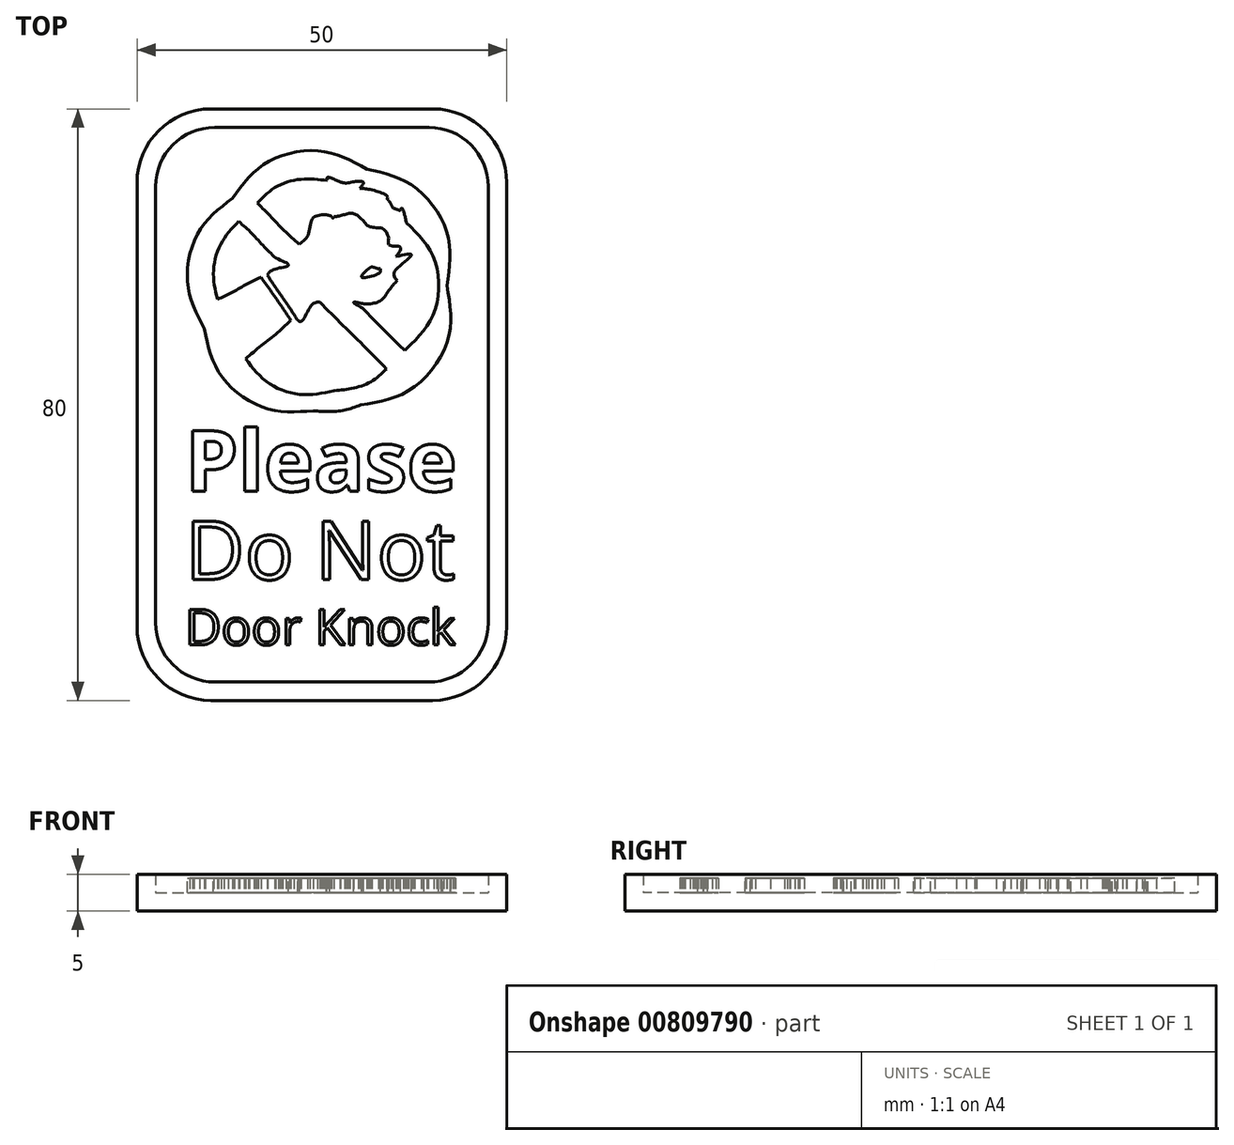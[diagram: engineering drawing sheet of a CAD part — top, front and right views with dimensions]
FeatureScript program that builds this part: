
annotation { "Feature Type Name" : "Feature", "Feature Type Description" : "" }
export const myFeature = defineFeature(function(context is Context, id is Id, definition is map)
    precondition{}
    {
        {
            var Q0;
            Q0=qCreatedBy(makeId("Top.planeOp"),FACE);
            var sketch = newSketch(context, id + "F0", { "sketchPlane" : qUnion([Q0])});
            skLineSegment(sketch, "E0.bottom", {"start": v(-25, 25) * mm, "end": v(25, 25) * mm});
            skLineSegment(sketch, "E0.top", {"start": v(-25, -55) * mm, "end": v(25, -55) * mm});
            skLineSegment(sketch, "E0.left", {"start": v(-25, 25) * mm, "end": v(-25, -55) * mm});
            skLineSegment(sketch, "E0.right", {"start": v(25, 25) * mm, "end": v(25, -55) * mm});
            skLineSegment(sketch, "E1", {"start": v(-25, 0) * mm, "end": v(25, 0) * mm});
            skSolve(sketch);
        }
        {
            var Q0;
            Q0 = qSketchRegion(id + "F0", true);
            extrude(context, id + "F1", {"entities" : qUnion([Q0]), "depth" : 5 * mm, "offsetDistance" : 25 * mm});
        }
        {
            var Q0;
            {var subQ0=sQuery(id+"F0.wireOp",EDGE,"E0.left");var subQ1=sQuery(id+"F0.wireOp",EDGE,"E0.top");var subQ2=sQuery(id+"F0.wireOp",EDGE,"E0.right");var subQ3=sQuery(id+"F0.wireOp",EDGE,"E0.bottom");Q0=makeQuery(id+"F8.boolean.opBoolean","SPLIT",FACE,{"disambiguationData":[TD([makeQuery(id+"F1.opExtrude","SWEPT_FACE",FACE,{"disambiguationData":[OSD([subQ3])]})])],"derivedFrom":makeQuery(id+"F1.opExtrude","CAP_FACE",FACE,{"disambiguationData":[OSD([subQ3,subQ1,subQ0,subQ2])],"isStart":false})});}
            shell(context, id + "F2", {"entities" : qUnion([Q0]), "thickness" : 2.5 * mm});
        }
        {
            var Q0;
            Q0=makeQuery(id+"F2.opShell","OFFSET_FACE",FACE,{"disambiguationData":[OSD([sQuery(id+"F0.wireOp",EDGE,"E0.bottom"),sQuery(id+"F0.wireOp",EDGE,"E0.top"),sQuery(id+"F0.wireOp",EDGE,"E0.left"),sQuery(id+"F0.wireOp",EDGE,"E0.right")])]});
            var sketch = newSketch(context, id + "F3", { "sketchPlane" : qUnion([Q0])});
            skText(sketch, "E2", { "text": "Please", "fontName": "OpenSans-Bold.ttf"});
            skText(sketch, "E3", { "text": "Do Not", "fontName": "OpenSans-Regular.ttf"});
            skText(sketch, "E4", { "text": "Door Knock", "fontName": "OpenSans-Regular.ttf"});
            const initialGuessF3  = {"E2": [-0.0185, -0.0267, 1, 0, 0.00823], "E3": [-0.0185, -0.03865, 1, 0, 0.00796], "E4": [-0.0185, -0.0475, 1, 0, 0.00485]};
            skSetInitialGuess(sketch, initialGuessF3);
            skSolve(sketch);
        }
        {
            var Q0;
            Q0 = qSketchRegion(id + "F3", true);
            extrude(context, id + "F4", {"entities" : qUnion([Q0]), "operationType" : NewBodyOperationType.ADD, "depth" : 2 * mm, "offsetDistance" : 25 * mm});
        }
        {
            var Q0;
            Q0=makeQuery(id+"F2.opShell","OFFSET_EDGE",EDGE,{"disambiguationData":[OSD([sQuery(id+"F0.wireOp",EDGE,"E0.bottom"),sQuery(id+"F0.wireOp",EDGE,"E0.left")])]});
            var Q1;
            Q1=makeQuery(id+"F2.opShell","OFFSET_EDGE",EDGE,{"disambiguationData":[OSD([sQuery(id+"F0.wireOp",EDGE,"E0.bottom"),sQuery(id+"F0.wireOp",EDGE,"E0.right")])]});
            var Q2;
            Q2=makeQuery(id+"F2.opShell","OFFSET_EDGE",EDGE,{"disambiguationData":[OSD([sQuery(id+"F0.wireOp",EDGE,"E0.top"),sQuery(id+"F0.wireOp",EDGE,"E0.right")])]});
            var Q3;
            Q3=makeQuery(id+"F2.opShell","OFFSET_EDGE",EDGE,{"disambiguationData":[OSD([sQuery(id+"F0.wireOp",EDGE,"E0.top"),sQuery(id+"F0.wireOp",EDGE,"E0.left")])]});
            fillet(context, id + "F5", {"entities" : qUnion([Q0, Q1, Q2, Q3]), "radius" : 8 * mm, "tangentPropagation" : true, "allowEdgeOverflow" : false});
        }
        {
            var Q0;
            Q0=makeQuery(id+"F1.opExtrude","SWEPT_EDGE",EDGE,{"disambiguationData":[OSD([sQuery(id+"F0.wireOp",EDGE,"E0.bottom"),sQuery(id+"F0.wireOp",EDGE,"E0.left")])]});
            var Q1;
            Q1=makeQuery(id+"F1.opExtrude","SWEPT_EDGE",EDGE,{"disambiguationData":[OSD([sQuery(id+"F0.wireOp",EDGE,"E0.top"),sQuery(id+"F0.wireOp",EDGE,"E0.left")])]});
            var Q2;
            Q2=makeQuery(id+"F1.opExtrude","SWEPT_EDGE",EDGE,{"disambiguationData":[OSD([sQuery(id+"F0.wireOp",EDGE,"E0.top"),sQuery(id+"F0.wireOp",EDGE,"E0.right")])]});
            var Q3;
            Q3=makeQuery(id+"F1.opExtrude","SWEPT_EDGE",EDGE,{"disambiguationData":[OSD([sQuery(id+"F0.wireOp",EDGE,"E0.bottom"),sQuery(id+"F0.wireOp",EDGE,"E0.right")])]});
            fillet(context, id + "F6", {"entities" : qUnion([Q0, Q1, Q2, Q3]), "radius" : 10 * mm, "tangentPropagation" : true, "allowEdgeOverflow" : false});
        }
        {
            var Q0;
            {var subQ0=sQuery(id+"F0.wireOp",EDGE,"E0.bottom");var subQ1=sQuery(id+"F0.wireOp",EDGE,"E0.top");var subQ2=sQuery(id+"F0.wireOp",EDGE,"E0.left");var subQ3=sQuery(id+"F0.wireOp",EDGE,"E0.right");Q0=makeQuery(id+"F4.boolean.opBoolean","SPLIT",FACE,{"disambiguationData":[TD([makeQuery(id+"F2.opShell","OFFSET_FACE",FACE,{"disambiguationData":[OSD([subQ0])]})])],"derivedFrom":makeQuery(id+"F2.opShell","OFFSET_FACE",FACE,{"disambiguationData":[OSD([subQ0,subQ1,subQ2,subQ3])]})});}
            var sketch = newSketch(context, id + "F7", { "sketchPlane" : qUnion([Q0])});
            skFitSpline(sketch, "E5", {"points": [v(-1.15, -15.83) * mm, v(-7.68, -15.45) * mm, v(-13.72, -10.92) * mm, v(-15.9, -4.75) * mm]});
            skFitSpline(sketch, "E6", {"points": [v(-15.9, -4.75) * mm, v(-18.13, 1.23) * mm, v(-16.62, 8.4) * mm, v(-12.09, 12.91) * mm]});
            skFitSpline(sketch, "E7", {"points": [v(-12.09, 12.91) * mm, v(-7.52, 17.7) * mm, v(-0.04, 19.3) * mm, v(6.1, 16.86) * mm]});
            skFitSpline(sketch, "E8", {"points": [v(6.1, 16.86) * mm, v(12.48, 14.48) * mm, v(17.02, 7.93) * mm, v(16.92, 1.1) * mm]});
            skFitSpline(sketch, "E9", {"points": [v(16.92, 1.1) * mm, v(17.08, -6.06) * mm, v(12.08, -12.9) * mm, v(5.25, -15.03) * mm]});
            skFitSpline(sketch, "E10", {"points": [v(5.25, -15.03) * mm, v(3.2, -15.72) * mm, v(1, -15.94) * mm, v(-1.15, -15.83) * mm]});
            skFitSpline(sketch, "E11", {"points": [v(1.66, -13.11) * mm, v(4.22, -12.79) * mm, v(6.74, -11.82) * mm, v(8.74, -10.18) * mm]});
            skFitSpline(sketch, "E12", {"points": [v(8.74, -10.18) * mm, v(5.76, -7.13) * mm, v(2.73, -4.14) * mm, v(-0.28, -1.12) * mm]});
            skFitSpline(sketch, "E13", {"points": [v(-0.28, -1.12) * mm, v(-1.38, -1.54) * mm, v(-2.81, -3.75) * mm, v(-3.77, -2.79) * mm]});
            skFitSpline(sketch, "E14", {"points": [v(-3.77, -2.79) * mm, v(-4.97, -1.02) * mm, v(-6.2, 0.74) * mm, v(-7.36, 2.53) * mm]});
            skFitSpline(sketch, "E15", {"points": [v(-7.36, 2.53) * mm, v(-6.5, 3.29) * mm, v(-4.52, 3.85) * mm, v(-6.24, 4.84) * mm]});
            skFitSpline(sketch, "E16", {"points": [v(-6.24, 4.84) * mm, v(-7.91, 6.47) * mm, v(-9.53, 8.22) * mm, v(-11.25, 9.78) * mm]});
            skFitSpline(sketch, "E17", {"points": [v(-11.25, 9.78) * mm, v(-13.58, 6.88) * mm, v(-14.66, 2.96) * mm, v(-14.13, -0.73) * mm]});
            skFitSpline(sketch, "E18", {"points": [v(-14.13, -0.73) * mm, v(-12.15, 0.15) * mm, v(-10.22, 1.3) * mm, v(-8.24, 2.23) * mm]});
            skFitSpline(sketch, "E19", {"points": [v(-8.24, 2.23) * mm, v(-6.85, 0.32) * mm, v(-5.5, -1.63) * mm, v(-4.19, -3.6) * mm]});
            skFitSpline(sketch, "E20", {"points": [v(-4.19, -3.6) * mm, v(-6.16, -5.4) * mm, v(-8.27, -7.06) * mm, v(-10.3, -8.8) * mm]});
            skFitSpline(sketch, "E21", {"points": [v(-10.3, -8.8) * mm, v(-7.27, -12.03) * mm, v(-2.72, -13.62) * mm, v(1.66, -13.11) * mm]});
            skFitSpline(sketch, "E22", {"points": [v(11.49, -7.4) * mm, v(15.19, -2.53) * mm, v(15.18, 4.74) * mm, v(11.44, 9.59) * mm]});
            skFitSpline(sketch, "E23", {"points": [v(11.44, 9.59) * mm, v(10.73, 11.53) * mm, v(9.63, 7.9) * mm, v(8.8, 9.37) * mm]});
            skFitSpline(sketch, "E24", {"points": [v(8.8, 9.37) * mm, v(9.6, 10.06) * mm, v(11.15, 10.8) * mm, v(9.6, 11.61) * mm]});
            skFitSpline(sketch, "E25", {"points": [v(9.6, 11.61) * mm, v(8.73, 12.84) * mm, v(7.9, 12.6) * mm, v(7.5, 11.2) * mm]});
            skFitSpline(sketch, "E26", {"points": [v(7.5, 11.2) * mm, v(7.16, 9.77) * mm, v(5.86, 11.26) * mm, v(7.04, 11.84) * mm]});
            skFitSpline(sketch, "E27", {"points": [v(7.04, 11.84) * mm, v(8.9, 13.12) * mm, v(5.97, 14.2) * mm, v(5.05, 14.22) * mm]});
            skFitSpline(sketch, "E28", {"points": [v(5.05, 14.22) * mm, v(4.74, 13.41) * mm, v(4.88, 10.93) * mm, v(3.78, 11.64) * mm]});
            skFitSpline(sketch, "E29", {"points": [v(3.78, 11.64) * mm, v(4, 12.9) * mm, v(5.64, 15.04) * mm, v(3.29, 14.95) * mm]});
            skFitSpline(sketch, "E30", {"points": [v(3.29, 14.95) * mm, v(2.26, 15.22) * mm, v(0.73, 15.72) * mm, v(1.4, 14.04) * mm]});
            skFitSpline(sketch, "E31", {"points": [v(1.4, 14.04) * mm, v(1.78, 13.25) * mm, v(1.54, 10.24) * mm, v(0.88, 11.92) * mm]});
            skFitSpline(sketch, "E32", {"points": [v(0.88, 11.92) * mm, v(0.9, 13.04) * mm, v(0.9, 14.17) * mm, v(0.92, 15.29) * mm]});
            skFitSpline(sketch, "E33", {"points": [v(0.92, 15.29) * mm, v(-2.5, 15.51) * mm, v(-6.08, 14.5) * mm, v(-8.7, 12.29) * mm]});
            skFitSpline(sketch, "E34", {"points": [v(-8.7, 12.29) * mm, v(-6.87, 10.39) * mm, v(-5.03, 8.48) * mm, v(-3.08, 6.7) * mm]});
            skFitSpline(sketch, "E35", {"points": [v(-3.08, 6.7) * mm, v(-1.85, 8) * mm, v(-1.25, 10.2) * mm, v(0.6, 10.7) * mm]});
            skFitSpline(sketch, "E36", {"points": [v(0.6, 10.7) * mm, v(2.2, 10.48) * mm, v(4.07, 10.9) * mm, v(5.48, 10.01) * mm]});
            skFitSpline(sketch, "E37", {"points": [v(5.48, 10.01) * mm, v(6.57, 9.04) * mm, v(8.26, 8.8) * mm, v(9.05, 7.52) * mm]});
            skFitSpline(sketch, "E38", {"points": [v(9.05, 7.52) * mm, v(9.16, 6.57) * mm, v(10.6, 6.33) * mm, v(10.04, 5.04) * mm]});
            skFitSpline(sketch, "E39", {"points": [v(10.04, 5.04) * mm, v(12.12, 5.22) * mm, v(9.8, 2.93) * mm, v(10.2, 1.8) * mm]});
            skFitSpline(sketch, "E40", {"points": [v(10.2, 1.8) * mm, v(9.18, 0.6) * mm, v(7.95, -0.91) * mm, v(6.4, -1.37) * mm]});
            skFitSpline(sketch, "E41", {"points": [v(6.4, -1.37) * mm, v(5.67, -1.36) * mm, v(4.32, -1.15) * mm, v(5.5, -1.97) * mm]});
            skFitSpline(sketch, "E42", {"points": [v(5.5, -1.97) * mm, v(7.4, -3.88) * mm, v(9.3, -5.8) * mm, v(11.24, -7.68) * mm]});
            skLineSegment(sketch, "E43", {"start": v(11.24, -7.68) * mm, "end": v(11.49, -7.4) * mm});
            skFitSpline(sketch, "E44", {"points": [v(6.6, 3.6) * mm, v(5.43, 2.24) * mm, v(7.79, 2.81) * mm, v(7.9, 3.36) * mm]});
            skFitSpline(sketch, "E45", {"points": [v(7.9, 3.36) * mm, v(7.47, 3.43) * mm, v(7.04, 3.59) * mm, v(6.6, 3.6) * mm]});
            skSolve(sketch);
        }
        {
            var Q0;
            Q0=makeQuery(id+"F7.imprint","IMPRINT",FACE,{"disambiguationData":[TD([[makeQuery(id+"F7.imprint","IMPRINT",EDGE,{"derivedFrom":sQuery(id+"F7.wireOp",EDGE,"E5")}),-1.0]])]});
            extrude(context, id + "F8", {"entities" : qUnion([Q0]), "operationType" : NewBodyOperationType.ADD, "depth" : 2 * mm, "offsetDistance" : 25 * mm});
        }
    });
